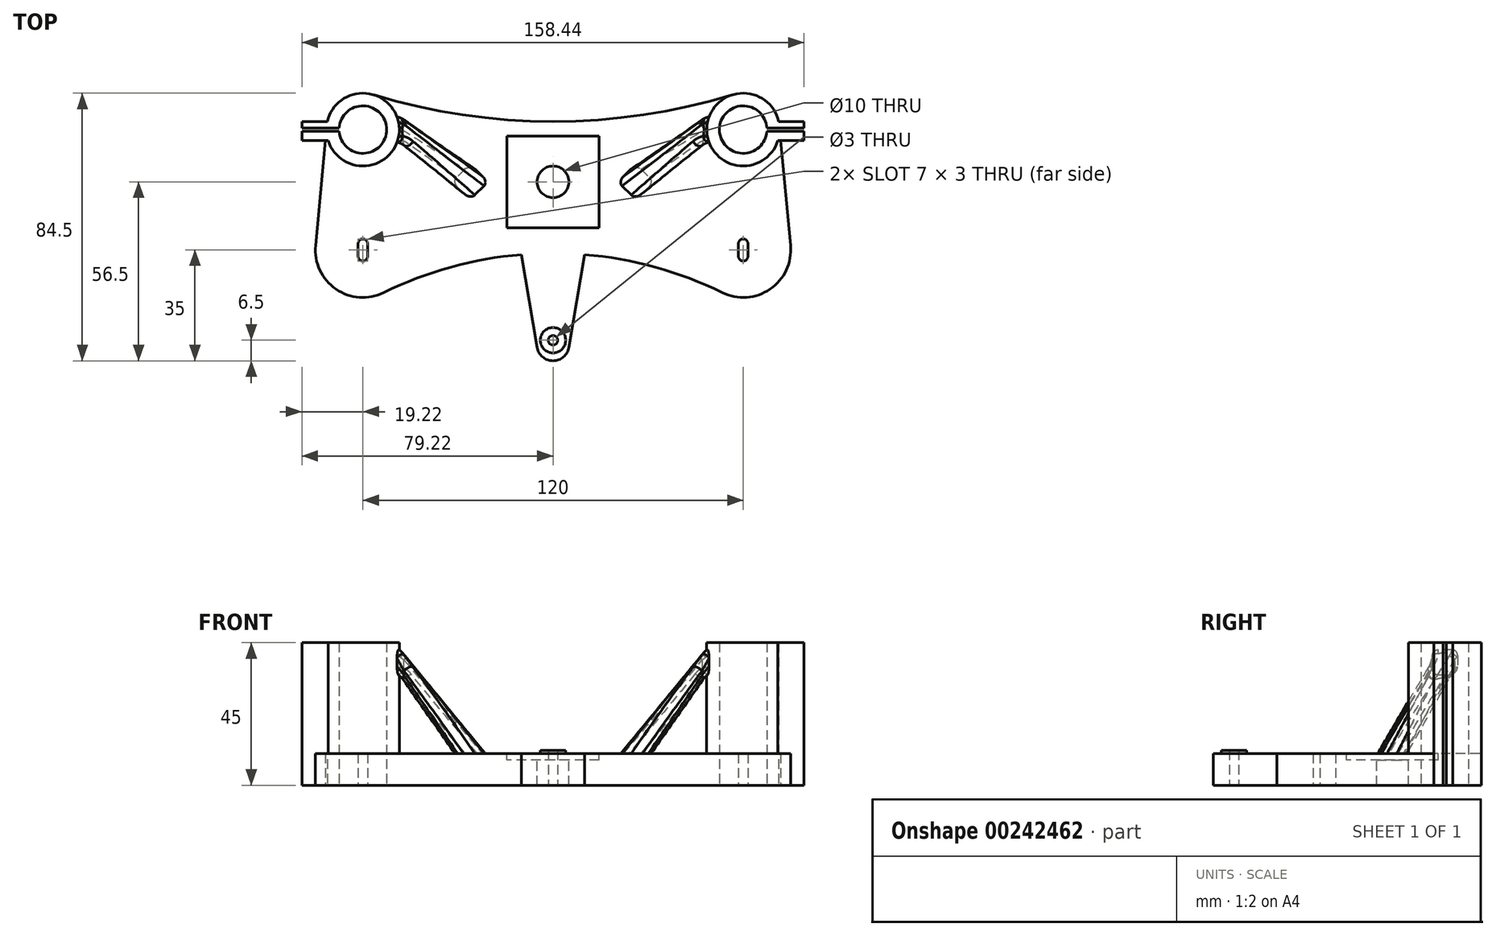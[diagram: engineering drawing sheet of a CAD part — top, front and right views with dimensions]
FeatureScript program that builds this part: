
annotation { "Feature Type Name" : "Feature", "Feature Type Description" : "" }
export const myFeature = defineFeature(function(context is Context, id is Id, definition is map)
    precondition{}
    {
        {
            var Q0;
            Q0=qCreatedBy(makeId("Top.planeOp"),FACE);
            var sketch = newSketch(context, id + "F0", { "sketchPlane" : qUnion([Q0])});
            skArc(sketch, "E0", {"start": v(-74.93, -36.6) * mm, "mid": v(-68.51, -50.35) * mm, "end": v(-53.38, -51.46) * mm});
            skArc(sketch, "E1", {"start": v(53.38, -51.46) * mm, "mid": v(68.51, -50.35) * mm, "end": v(74.93, -36.6) * mm});
            skLineSegment(sketch, "E2", {"start": v(-60, -36) * mm, "end": v(-60, -40) * mm, "construction": true});
            skLineSegment(sketch, "E3", {"start": v(60, -36) * mm, "end": v(60, -40) * mm, "construction": true});
            skArc(sketch, "E4.0.startCap", {"start": v(58.5, -36) * mm, "mid": v(60, -34.5) * mm, "end": v(61.5, -36) * mm});
            skArc(sketch, "E4.0.endCap", {"start": v(61.5, -40) * mm, "mid": v(60, -41.5) * mm, "end": v(58.5, -40) * mm});
            skLineSegment(sketch, "E4.0.left", {"start": v(61.5, -36) * mm, "end": v(61.5, -40) * mm});
            skLineSegment(sketch, "E4.0.right", {"start": v(58.5, -36) * mm, "end": v(58.5, -40) * mm});
            skArc(sketch, "E5.0.startCap", {"start": v(-61.5, -36) * mm, "mid": v(-60, -34.5) * mm, "end": v(-58.5, -36) * mm});
            skArc(sketch, "E5.0.endCap", {"start": v(-58.5, -40) * mm, "mid": v(-60, -41.5) * mm, "end": v(-61.5, -40) * mm});
            skLineSegment(sketch, "E5.0.left", {"start": v(-58.5, -36) * mm, "end": v(-58.5, -40) * mm});
            skLineSegment(sketch, "E5.0.right", {"start": v(-61.5, -36) * mm, "end": v(-61.5, -40) * mm});
            skPoint(sketch, "E6", {"position": v(0, -39.46) * mm});
            skLineSegment(sketch, "E7", {"start": v(-10, -39.46) * mm, "end": v(10, -39.46) * mm, "construction": true});
            skLineSegment(sketch, "E8", {"start": v(-10, -39.46) * mm, "end": v(-5, -68.78) * mm});
            skLineSegment(sketch, "E9", {"start": v(10, -39.46) * mm, "end": v(5, -68.78) * mm});
            skArc(sketch, "E10", {"start": v(-5, -68.78) * mm, "mid": v(0, -73) * mm, "end": v(5, -68.78) * mm});
            skLineSegment(sketch, "E11", {"start": v(-5, -68.78) * mm, "end": v(5, -68.78) * mm, "construction": true});
            skCircle(sketch, "E12", {"center": v(-60, 0) * mm, "radius": 11.5 * mm});
            skCircle(sketch, "E13", {"center": v(60, 0) * mm, "radius": 11.5 * mm});
            skLineSegment(sketch, "E14", {"start": v(-60, 0) * mm, "end": v(60, 0) * mm, "construction": true});
            skLineSegment(sketch, "E15", {"start": v(0, 0) * mm, "end": v(0, -176.53) * mm, "construction": true});
            skLineSegment(sketch, "E16", {"start": v(-60, -38) * mm, "end": v(60, -38) * mm, "construction": true});
            skLineSegment(sketch, "E17", {"start": v(-60, 0) * mm, "end": v(-60, 11.5) * mm, "construction": true});
            skLineSegment(sketch, "E18", {"start": v(60, 0) * mm, "end": v(60, 11.5) * mm, "construction": true});
            skArc(sketch, "E19", {"start": v(53.38, -51.46) * mm, "mid": v(0, -39.04) * mm, "end": v(-53.38, -51.46) * mm});
            skLineSegment(sketch, "E20", {"start": v(-56.65, 11) * mm, "end": v(56.65, 11) * mm, "construction": true});
            skArc(sketch, "E21", {"start": v(-56.65, 11) * mm, "mid": v(0, 2.56) * mm, "end": v(56.65, 11) * mm});
            skLineSegment(sketch, "E22", {"start": v(-60, 0) * mm, "end": v(-71.5, 0) * mm, "construction": true});
            skLineSegment(sketch, "E23", {"start": v(60, 0) * mm, "end": v(71.5, 0) * mm, "construction": true});
            skLineSegment(sketch, "E24", {"start": v(-71.5, 0) * mm, "end": v(-74.93, -36.6) * mm});
            skLineSegment(sketch, "E25", {"start": v(71.5, 0) * mm, "end": v(74.93, -36.6) * mm});
            skLineSegment(sketch, "E26", {"start": v(-71.22, 2.5) * mm, "end": v(-79.22, 2.5) * mm});
            skLineSegment(sketch, "E27", {"start": v(-79.22, 2.5) * mm, "end": v(-79.22, 0.5) * mm});
            skLineSegment(sketch, "E28", {"start": v(-79.22, 0.5) * mm, "end": v(-60, 0.5) * mm});
            skLineSegment(sketch, "E29", {"start": v(-60, 0.5) * mm, "end": v(-60, -0.5) * mm});
            skLineSegment(sketch, "E30", {"start": v(-60, -0.5) * mm, "end": v(-79.22, -0.5) * mm});
            skLineSegment(sketch, "E31", {"start": v(-79.22, -0.5) * mm, "end": v(-79.22, -3.5) * mm});
            skLineSegment(sketch, "E32", {"start": v(-79.22, -3.5) * mm, "end": v(-70.95, -3.5) * mm});
            skLineSegment(sketch, "E33", {"start": v(71.22, 2.5) * mm, "end": v(79.22, 2.5) * mm});
            skLineSegment(sketch, "E34", {"start": v(79.22, 2.5) * mm, "end": v(79.22, 0.5) * mm});
            skLineSegment(sketch, "E35", {"start": v(79.22, 0.5) * mm, "end": v(60, 0.5) * mm});
            skLineSegment(sketch, "E36", {"start": v(60, 0.5) * mm, "end": v(60, -0.5) * mm});
            skLineSegment(sketch, "E37", {"start": v(60, -0.5) * mm, "end": v(79.22, -0.5) * mm});
            skLineSegment(sketch, "E38", {"start": v(79.22, -0.5) * mm, "end": v(79.22, -3.5) * mm});
            skLineSegment(sketch, "E39", {"start": v(79.22, -3.5) * mm, "end": v(70.95, -3.5) * mm});
            skSolve(sketch);
        }
        {
            var Q0;
            Q0 = qSketchRegion(id + "F0", true);
            var Q1;
            Q1=makeQuery(id+"F0.imprint","IMPRINT",FACE,{"disambiguationData":[TD([[makeQuery(id+"F0.imprint","IMPRINT",EDGE,{"derivedFrom":sQuery(id+"F0.wireOp",EDGE,"LKLDyHX9-gXCm-k2y8-ggSg-qPZ12blG1iR6.bottom")}),-1.0]])]});
            extrude(context, id + "F1", {"entities" : qUnion([Q0, Q1]), "depth" : 10 * mm});
        }
        {
            var Q0;
            {var subQ0=sQuery(id+"F0.wireOp",EDGE,"E12");var subQ1=makeQuery(id+"F0.imprint","INTERSECT",VERTEX,{"derivedFrom":[subQ0,sQuery(id+"F0.wireOp",EDGE,"E21")]});Q0=makeQuery(id+"F0.imprint","IMPRINT",FACE,{"disambiguationData":[TD([[makeQuery(id+"F0.imprint","IMPRINT",EDGE,{"disambiguationData":[TD([[subQ1,-1.0]])],"derivedFrom":subQ0}),1.0]])]});}
            var Q1;
            {var subQ0=sQuery(id+"F0.wireOp",EDGE,"E13");var subQ1=makeQuery(id+"F0.imprint","INTERSECT",VERTEX,{"derivedFrom":[subQ0,sQuery(id+"F0.wireOp",EDGE,"E21")]});Q1=makeQuery(id+"F0.imprint","IMPRINT",FACE,{"disambiguationData":[TD([[makeQuery(id+"F0.imprint","IMPRINT",EDGE,{"disambiguationData":[TD([[subQ1,1.0]])],"derivedFrom":subQ0}),1.0]])]});}
            var Q2;
            {var subQ0=sQuery(id+"F0.wireOp",EDGE,"E26");Q2=makeQuery(id+"F0.imprint","IMPRINT",FACE,{"disambiguationData":[TD([[makeQuery(id+"F0.imprint","IMPRINT",EDGE,{"derivedFrom":subQ0}),1.0]])]});}
            var Q3;
            {var subQ4=sQuery(id+"F0.wireOp",EDGE,"E31");Q3=makeQuery(id+"F0.imprint","IMPRINT",FACE,{"disambiguationData":[TD([[makeQuery(id+"F0.imprint","IMPRINT",EDGE,{"derivedFrom":subQ4}),1.0]])]});}
            var Q4;
            {var subQ0=sQuery(id+"F0.wireOp",EDGE,"E32");var subQ1=sQuery(id+"F0.wireOp",EDGE,"E12");var subQ2=makeQuery(id+"F0.imprint","INTERSECT",VERTEX,{"derivedFrom":[subQ1,subQ0]});Q4=makeQuery(id+"F0.imprint","IMPRINT",FACE,{"disambiguationData":[TD([[makeQuery(id+"F0.imprint","IMPRINT",EDGE,{"disambiguationData":[TD([[subQ2,1.0]])],"derivedFrom":subQ1}),-1.0]])]});}
            var Q5;
            {var subQ0=sQuery(id+"F0.wireOp",EDGE,"E39");var subQ1=sQuery(id+"F0.wireOp",EDGE,"E13");var subQ2=makeQuery(id+"F0.imprint","INTERSECT",VERTEX,{"derivedFrom":[subQ1,subQ0]});Q5=makeQuery(id+"F0.imprint","IMPRINT",FACE,{"disambiguationData":[TD([[makeQuery(id+"F0.imprint","IMPRINT",EDGE,{"disambiguationData":[TD([[subQ2,-1.0]])],"derivedFrom":subQ1}),-1.0]])]});}
            var Q6;
            {var subQ5=sQuery(id+"F0.wireOp",EDGE,"E38");Q6=makeQuery(id+"F0.imprint","IMPRINT",FACE,{"disambiguationData":[TD([[makeQuery(id+"F0.imprint","IMPRINT",EDGE,{"derivedFrom":subQ5}),-1.0]])]});}
            var Q7;
            {var subQ0=sQuery(id+"F0.wireOp",EDGE,"E33");Q7=makeQuery(id+"F0.imprint","IMPRINT",FACE,{"disambiguationData":[TD([[makeQuery(id+"F0.imprint","IMPRINT",EDGE,{"derivedFrom":subQ0}),-1.0]])]});}
            extrude(context, id + "F2", {"entities" : qUnion([Q0, Q1, Q2, Q3, Q4, Q5, Q6, Q7]), "operationType" : NewBodyOperationType.ADD, "depth" : 45 * mm});
        }
        {
            var Q0;
            Q0=makeQuery(id+"F1.opExtrude","CAP_FACE",FACE,{"disambiguationData":[OSD([sQuery(id+"F0.wireOp",EDGE,"47a20475-fb0e-48b2-b259-d4306b60a212"),sQuery(id+"F0.wireOp",EDGE,"11a2ab9f-6c47-45e5-a705-5a51ec2baa43"),sQuery(id+"F0.wireOp",EDGE,"7d5b429a-6b9c-4788-a966-0b9b0a1ef2b6"),sQuery(id+"F0.wireOp",EDGE,"E0"),sQuery(id+"F0.wireOp",EDGE,"E1"),sQuery(id+"F0.wireOp",EDGE,"E4.0.startCap"),sQuery(id+"F0.wireOp",EDGE,"E4.0.endCap"),sQuery(id+"F0.wireOp",EDGE,"E4.0.left"),sQuery(id+"F0.wireOp",EDGE,"E4.0.right"),sQuery(id+"F0.wireOp",EDGE,"E5.0.startCap"),sQuery(id+"F0.wireOp",EDGE,"E5.0.endCap"),sQuery(id+"F0.wireOp",EDGE,"E5.0.left"),sQuery(id+"F0.wireOp",EDGE,"E5.0.right"),sQuery(id+"F0.wireOp",EDGE,"ed3533a6-83fa-43d6-bacc-5741e4b977db"),sQuery(id+"F0.wireOp",EDGE,"E8"),sQuery(id+"F0.wireOp",EDGE,"E9"),sQuery(id+"F0.wireOp",EDGE,"E10"),sQuery(id+"F0.wireOp",EDGE,"E12"),sQuery(id+"F0.wireOp",EDGE,"E13")])],"isStart":true});
            var sketch = newSketch(context, id + "F3", { "sketchPlane" : qUnion([Q0])});
            skCircle(sketch, "E40", {"center": v(-60, 0) * mm, "radius": 7.5 * mm});
            skCircle(sketch, "E41", {"center": v(60, 0) * mm, "radius": 7.5 * mm});
            skSolve(sketch);
        }
        {
            var Q0;
            Q0 = qSketchRegion(id + "F3", true);
            var Q1;
            {var subQ0=sQuery(id+"F0.wireOp",EDGE,"E29");Q1=makeQuery(id+"F0.imprint","IMPRINT",FACE,{"disambiguationData":[TD([[makeQuery(id+"F0.imprint","IMPRINT",EDGE,{"derivedFrom":subQ0}),-1.0]])]});}
            var Q2;
            {var subQ0=sQuery(id+"F0.wireOp",EDGE,"E24");var subQ1=sQuery(id+"F0.wireOp",EDGE,"E12");var subQ2=makeQuery(id+"F0.imprint","INTERSECT",VERTEX,{"derivedFrom":[subQ1,subQ0]});Q2=makeQuery(id+"F0.imprint","IMPRINT",FACE,{"disambiguationData":[TD([[makeQuery(id+"F0.imprint","IMPRINT",EDGE,{"disambiguationData":[TD([[subQ2,-1.0]])],"derivedFrom":subQ1}),-1.0]])]});}
            var Q3;
            {var subQ0=sQuery(id+"F0.wireOp",EDGE,"E36");Q3=makeQuery(id+"F0.imprint","IMPRINT",FACE,{"disambiguationData":[TD([[makeQuery(id+"F0.imprint","IMPRINT",EDGE,{"derivedFrom":subQ0}),1.0]])]});}
            var Q4;
            {var subQ0=sQuery(id+"F0.wireOp",EDGE,"E25");var subQ1=sQuery(id+"F0.wireOp",EDGE,"E13");var subQ2=makeQuery(id+"F0.imprint","INTERSECT",VERTEX,{"derivedFrom":[subQ1,subQ0]});Q4=makeQuery(id+"F0.imprint","IMPRINT",FACE,{"disambiguationData":[TD([[makeQuery(id+"F0.imprint","IMPRINT",EDGE,{"disambiguationData":[TD([[subQ2,1.0]])],"derivedFrom":subQ1}),-1.0]])]});}
            extrude(context, id + "F4", {"entities" : qUnion([Q0, Q1, Q2, Q3, Q4]), "operationType" : NewBodyOperationType.REMOVE, "endBound" : BoundingType.THROUGH_ALL, "oppositeDirection" : true, "depth" : 25 * mm});
        }
        {
            var Q0;
            Q0=makeQuery(id+"F1.opExtrude","CAP_FACE",FACE,{"disambiguationData":[OSD([sQuery(id+"F0.wireOp",EDGE,"E0"),sQuery(id+"F0.wireOp",EDGE,"E1"),sQuery(id+"F0.wireOp",EDGE,"E4.0.startCap"),sQuery(id+"F0.wireOp",EDGE,"E4.0.endCap"),sQuery(id+"F0.wireOp",EDGE,"E4.0.left"),sQuery(id+"F0.wireOp",EDGE,"E4.0.right"),sQuery(id+"F0.wireOp",EDGE,"E5.0.startCap"),sQuery(id+"F0.wireOp",EDGE,"E5.0.endCap"),sQuery(id+"F0.wireOp",EDGE,"E5.0.left"),sQuery(id+"F0.wireOp",EDGE,"E5.0.right"),sQuery(id+"F0.wireOp",EDGE,"E8"),sQuery(id+"F0.wireOp",EDGE,"E9"),sQuery(id+"F0.wireOp",EDGE,"E10"),sQuery(id+"F0.wireOp",EDGE,"E12"),sQuery(id+"F0.wireOp",EDGE,"E13"),sQuery(id+"F0.wireOp",EDGE,"E19"),sQuery(id+"F0.wireOp",EDGE,"E21"),sQuery(id+"F0.wireOp",EDGE,"E24"),sQuery(id+"F0.wireOp",EDGE,"E25")])],"isStart":false});
            var sketch = newSketch(context, id + "F5", { "sketchPlane" : qUnion([Q0])});
            skCircle(sketch, "E42", {"center": v(0, -16.5) * mm, "radius": 5 * mm});
            skLineSegment(sketch, "E43.bottom", {"start": v(14.5, -2) * mm, "end": v(-14.5, -2) * mm});
            skLineSegment(sketch, "E43.top", {"start": v(14.5, -31) * mm, "end": v(-14.5, -31) * mm});
            skLineSegment(sketch, "E43.left", {"start": v(14.5, -2) * mm, "end": v(14.5, -31) * mm});
            skLineSegment(sketch, "E43.right", {"start": v(-14.5, -2) * mm, "end": v(-14.5, -31) * mm});
            skSolve(sketch);
        }
        {
            var Q0;
            Q0=makeQuery(id+"F5.imprint","IMPRINT",FACE,{"disambiguationData":[TD([[makeQuery(id+"F5.imprint","IMPRINT",EDGE,{"derivedFrom":sQuery(id+"F5.wireOp",EDGE,"E42")}),1.0]])]});
            extrude(context, id + "F6", {"entities" : qUnion([Q0]), "operationType" : NewBodyOperationType.REMOVE, "endBound" : BoundingType.THROUGH_ALL, "oppositeDirection" : true, "depth" : 25 * mm});
        }
        {
            var Q0;
            Q0=makeQuery(id+"F5.imprint","IMPRINT",FACE,{"disambiguationData":[TD([[makeQuery(id+"F5.imprint","IMPRINT",EDGE,{"derivedFrom":sQuery(id+"F5.wireOp",EDGE,"E42")}),-1.0]])]});
            extrude(context, id + "F7", {"entities" : qUnion([Q0]), "operationType" : NewBodyOperationType.REMOVE, "oppositeDirection" : true, "depth" : 2 * mm});
        }
        {
            var Q0;
            Q0=qCreatedBy(makeId("Right.planeOp"),FACE);
            var sketch = newSketch(context, id + "F8", { "sketchPlane" : qUnion([Q0])});
            skLineSegment(sketch, "E44.bottom", {"start": v(-4, 42.81) * mm, "end": v(4, 42.81) * mm});
            skLineSegment(sketch, "E44.top", {"start": v(-4, 34.81) * mm, "end": v(4, 34.81) * mm});
            skLineSegment(sketch, "E44.left", {"start": v(-4, 42.81) * mm, "end": v(-4, 34.81) * mm});
            skLineSegment(sketch, "E44.right", {"start": v(4, 42.81) * mm, "end": v(4, 34.81) * mm});
            skPoint(sketch, "E45", {"position": v(0, 42.81) * mm});
            skSolve(sketch);
        }
        {
            var Q0;
            {var subQ0=sQuery(id+"F0.wireOp",EDGE,"E25");var subQ1=sQuery(id+"F0.wireOp",EDGE,"E1");var subQ2=sQuery(id+"F0.wireOp",EDGE,"E39");var subQ3=sQuery(id+"F0.wireOp",EDGE,"E12");var subQ4=sQuery(id+"F0.wireOp",EDGE,"E21");var subQ5=sQuery(id+"F0.wireOp",EDGE,"E19");var subQ6=sQuery(id+"F0.wireOp",EDGE,"E0");var subQ7=sQuery(id+"F0.wireOp",EDGE,"E8");var subQ8=sQuery(id+"F0.wireOp",EDGE,"E9");var subQ9=sQuery(id+"F0.wireOp",EDGE,"E13");var subQ10=sQuery(id+"F0.wireOp",EDGE,"E33");var subQ11=sQuery(id+"F0.wireOp",EDGE,"E26");var subQ12=sQuery(id+"F0.wireOp",EDGE,"E32");var subQ13=sQuery(id+"F0.wireOp",EDGE,"E10");var subQ14=sQuery(id+"F0.wireOp",EDGE,"E4.0.startCap");var subQ15=sQuery(id+"F0.wireOp",EDGE,"E4.0.endCap");var subQ16=sQuery(id+"F0.wireOp",EDGE,"E24");var subQ17=sQuery(id+"F0.wireOp",EDGE,"E5.0.right");var subQ18=sQuery(id+"F0.wireOp",EDGE,"E4.0.left");var subQ19=sQuery(id+"F0.wireOp",EDGE,"E4.0.right");var subQ20=sQuery(id+"F0.wireOp",EDGE,"E5.0.startCap");var subQ21=sQuery(id+"F0.wireOp",EDGE,"E5.0.endCap");var subQ22=sQuery(id+"F0.wireOp",EDGE,"E5.0.left");Q0=makeQuery(id+"F2.boolean.opBoolean","SPLIT",FACE,{"disambiguationData":[TD([makeQuery(id+"F1.opExtrude","SWEPT_FACE",FACE,{"disambiguationData":[OSD([subQ6])]})])],"derivedFrom":makeQuery(id+"F1.opExtrude","CAP_FACE",FACE,{"disambiguationData":[OSD([subQ6,subQ1,subQ14,subQ15,subQ18,subQ19,subQ20,subQ21,subQ22,subQ17,subQ7,subQ8,subQ13,subQ3,subQ9,subQ5,subQ4,subQ16,subQ0,subQ11,sQuery(id+"F0.wireOp",EDGE,"E27"),sQuery(id+"F0.wireOp",EDGE,"E28"),sQuery(id+"F0.wireOp",EDGE,"E30"),sQuery(id+"F0.wireOp",EDGE,"E31"),subQ12,subQ10,sQuery(id+"F0.wireOp",EDGE,"E34"),sQuery(id+"F0.wireOp",EDGE,"E35"),sQuery(id+"F0.wireOp",EDGE,"E37"),sQuery(id+"F0.wireOp",EDGE,"E38"),subQ2])],"isStart":false})});}
            var sketch = newSketch(context, id + "F9", { "sketchPlane" : qUnion([Q0])});
            skLineSegment(sketch, "E46.bottom", {"start": v(20.5, -16.5) * mm, "end": v(26.16, -10.84) * mm});
            skLineSegment(sketch, "E46.top", {"start": v(26.16, -22.16) * mm, "end": v(31.81, -16.5) * mm});
            skLineSegment(sketch, "E46.left", {"start": v(20.5, -16.5) * mm, "end": v(26.16, -22.16) * mm});
            skLineSegment(sketch, "E46.right", {"start": v(26.16, -10.84) * mm, "end": v(31.81, -16.5) * mm});
            skLineSegment(sketch, "E47", {"start": v(26.16, -22.16) * mm, "end": v(26.16, -10.84) * mm, "construction": true});
            skLineSegment(sketch, "E48.bottom", {"start": v(-26.16, -10.84) * mm, "end": v(-20.5, -16.5) * mm});
            skLineSegment(sketch, "E48.top", {"start": v(-31.81, -16.5) * mm, "end": v(-26.16, -22.16) * mm});
            skLineSegment(sketch, "E48.left", {"start": v(-26.16, -10.84) * mm, "end": v(-31.81, -16.5) * mm});
            skLineSegment(sketch, "E48.right", {"start": v(-20.5, -16.5) * mm, "end": v(-26.16, -22.16) * mm});
            skLineSegment(sketch, "E49", {"start": v(-26.16, -10.84) * mm, "end": v(-26.16, -22.16) * mm, "construction": true});
            skCircle(sketch, "E50", {"center": v(0, -66.5) * mm, "radius": 4 * mm});
            skCircle(sketch, "E51", {"center": v(0, -66.5) * mm, "radius": 1.5 * mm});
            skSolve(sketch);
        }
        {
            var Q0;
            Q0 = qSketchRegion(id + "F8", true);
            var Q1;
            {var subQ0=sQuery(id+"F0.wireOp",EDGE,"E13");Q1=makeQuery(id+"F2.boolean.opBoolean","MERGE",FACE,{"derivedFrom":[makeQuery(id+"F1.opExtrude","SWEPT_FACE",FACE,{"disambiguationData":[OSD([subQ0]),TDD([makeQuery(id+"F0.imprint","IMPRINT",EDGE,{"disambiguationData":[TD([[makeQuery(id+"F0.imprint","INTERSECT",VERTEX,{"derivedFrom":[subQ0,sQuery(id+"F0.wireOp",EDGE,"E21")]}),1.0]])],"derivedFrom":subQ0})])]}),makeQuery(id+"F2.opExtrude","SWEPT_FACE",FACE,{"disambiguationData":[OSD([subQ0])]})]});}
            var Q2;
            {var subQ0=sQuery(id+"F0.wireOp",EDGE,"E13");Q2=makeQuery(id+"F2.boolean.opBoolean","MERGE",FACE,{"derivedFrom":[makeQuery(id+"F1.opExtrude","SWEPT_FACE",FACE,{"disambiguationData":[OSD([subQ0]),TDD([makeQuery(id+"F0.imprint","IMPRINT",EDGE,{"disambiguationData":[TD([[makeQuery(id+"F0.imprint","INTERSECT",VERTEX,{"derivedFrom":[subQ0,sQuery(id+"F0.wireOp",EDGE,"E21")]}),1.0]])],"derivedFrom":subQ0})])]}),makeQuery(id+"F2.opExtrude","SWEPT_FACE",FACE,{"disambiguationData":[OSD([subQ0])]})]});}
            extrude(context, id + "F10", {"entities" : qUnion([Q0]), "operationType" : NewBodyOperationType.ADD, "endBound" : BoundingType.UP_TO_SURFACE, "endBoundEntityFace" : qUnion([Q1]), "depth" : 25 * mm, "hasSecondDirection" : true, "secondDirectionOppositeDirection" : false, "secondDirectionBoundEntityFace" : qUnion([Q2]), "secondDirectionDepth" : 48.3 * mm});
        }
        {
            var Q0;
            Q0=makeQuery(id+"F8.imprint","IMPRINT",FACE,{"disambiguationData":[TD([[makeQuery(id+"F8.imprint","IMPRINT",EDGE,{"derivedFrom":sQuery(id+"F8.wireOp",EDGE,"E44.bottom")}),-1.0]])]});
            var Q1;
            {var subQ0=sQuery(id+"F0.wireOp",EDGE,"E12");Q1=makeQuery(id+"F2.boolean.opBoolean","MERGE",FACE,{"derivedFrom":[makeQuery(id+"F1.opExtrude","SWEPT_FACE",FACE,{"disambiguationData":[OSD([subQ0]),TDD([makeQuery(id+"F0.imprint","IMPRINT",EDGE,{"disambiguationData":[TD([[makeQuery(id+"F0.imprint","INTERSECT",VERTEX,{"derivedFrom":[subQ0,sQuery(id+"F0.wireOp",EDGE,"E21")]}),-1.0]])],"derivedFrom":subQ0})])]}),makeQuery(id+"F2.opExtrude","SWEPT_FACE",FACE,{"disambiguationData":[OSD([subQ0])]})]});}
            extrude(context, id + "F11", {"entities" : qUnion([Q0]), "operationType" : NewBodyOperationType.ADD, "endBound" : BoundingType.UP_TO_SURFACE, "oppositeDirection" : true, "endBoundEntityFace" : qUnion([Q1]), "depth" : 46.6 * mm, "hasSecondDirection" : true, "secondDirectionOppositeDirection" : true, "secondDirectionDepth" : 48.3 * mm});
        }
        {
            var Q1;
            Q1=makeQuery(id+"F9.imprint","IMPRINT",FACE,{"disambiguationData":[TD([[makeQuery(id+"F9.imprint","IMPRINT",EDGE,{"derivedFrom":sQuery(id+"F9.wireOp",EDGE,"E46.bottom")}),-1.0]])]});
            var Q2;
            Q2=makeQuery(id+"F10.opExtrude","CAP_FACE",FACE,{"disambiguationData":[OSD([sQuery(id+"F8.wireOp",EDGE,"E44.bottom"),sQuery(id+"F8.wireOp",EDGE,"E44.top"),sQuery(id+"F8.wireOp",EDGE,"E44.left"),sQuery(id+"F8.wireOp",EDGE,"E44.right")])],"isStart":true});
            loft(context, id + "F12", {"operationType" : NewBodyOperationType.ADD, "sheetProfilesArray" : [{ "sheetProfileEntities" : qUnion([Q1]) }, { "sheetProfileEntities" : qUnion([Q2]) }]});
        }
        {
            var Q1;
            Q1=makeQuery(id+"F9.imprint","IMPRINT",FACE,{"disambiguationData":[TD([[makeQuery(id+"F9.imprint","IMPRINT",EDGE,{"derivedFrom":sQuery(id+"F9.wireOp",EDGE,"E48.bottom")}),-1.0]])]});
            var Q2;
            Q2=makeQuery(id+"F11.opExtrude","CAP_FACE",FACE,{"disambiguationData":[OSD([sQuery(id+"F8.wireOp",EDGE,"E44.bottom"),sQuery(id+"F8.wireOp",EDGE,"E44.top"),sQuery(id+"F8.wireOp",EDGE,"E44.left"),sQuery(id+"F8.wireOp",EDGE,"E44.right")])],"isStart":true});
            loft(context, id + "F13", {"operationType" : NewBodyOperationType.ADD, "sheetProfilesArray" : [{ "sheetProfileEntities" : qUnion([Q1]) }, { "sheetProfileEntities" : qUnion([Q2]) }]});
        }
        {
            var Q0;
            {var subQ0=sQuery(id+"F8.wireOp",EDGE,"E44.right");Q0=makeQuery(id+"F12.boolean.opBoolean","MERGE",EDGE,{"derivedFrom":[makeQuery(id+"F10.opExtrude","CAP_EDGE",EDGE,{"disambiguationData":[OSD([subQ0])],"isStart":true}),makeQuery(id+"F12.opLoft","MID_CAP_EDGE",EDGE,{"disambiguationData":[OSD([sQuery(id+"F8.wireOp",EDGE,"E44.bottom"),sQuery(id+"F8.wireOp",EDGE,"E44.top"),subQ0])],"capPos":1.0})]});}
            var Q1;
            {var subQ0=sQuery(id+"F8.wireOp",EDGE,"E44.left");Q1=makeQuery(id+"F12.boolean.opBoolean","MERGE",EDGE,{"derivedFrom":[makeQuery(id+"F10.opExtrude","CAP_EDGE",EDGE,{"disambiguationData":[OSD([subQ0])],"isStart":true}),makeQuery(id+"F12.opLoft","MID_CAP_EDGE",EDGE,{"disambiguationData":[OSD([sQuery(id+"F8.wireOp",EDGE,"E44.bottom"),sQuery(id+"F8.wireOp",EDGE,"E44.top"),subQ0])],"capPos":1.0})]});}
            var Q2;
            {var subQ0=sQuery(id+"F8.wireOp",EDGE,"E44.bottom");Q2=makeQuery(id+"F12.boolean.opBoolean","MERGE",EDGE,{"derivedFrom":[makeQuery(id+"F10.opExtrude","CAP_EDGE",EDGE,{"disambiguationData":[OSD([subQ0])],"isStart":true}),makeQuery(id+"F12.opLoft","MID_CAP_EDGE",EDGE,{"disambiguationData":[OSD([subQ0,sQuery(id+"F8.wireOp",EDGE,"E44.left"),sQuery(id+"F8.wireOp",EDGE,"E44.right")])],"capPos":1.0})]});}
            var Q3;
            {var subQ0=sQuery(id+"F8.wireOp",EDGE,"E44.bottom");Q3=makeQuery(id+"F13.boolean.opBoolean","MERGE",EDGE,{"derivedFrom":[makeQuery(id+"F11.opExtrude","CAP_EDGE",EDGE,{"disambiguationData":[OSD([subQ0])],"isStart":true}),makeQuery(id+"F13.opLoft","MID_CAP_EDGE",EDGE,{"disambiguationData":[OSD([subQ0,sQuery(id+"F8.wireOp",EDGE,"E44.left"),sQuery(id+"F8.wireOp",EDGE,"E44.right")])],"capPos":1.0})]});}
            var Q4;
            {var subQ0=sQuery(id+"F8.wireOp",EDGE,"E44.left");Q4=makeQuery(id+"F13.boolean.opBoolean","MERGE",EDGE,{"derivedFrom":[makeQuery(id+"F11.opExtrude","CAP_EDGE",EDGE,{"disambiguationData":[OSD([subQ0])],"isStart":true}),makeQuery(id+"F13.opLoft","MID_CAP_EDGE",EDGE,{"disambiguationData":[OSD([sQuery(id+"F8.wireOp",EDGE,"E44.bottom"),sQuery(id+"F8.wireOp",EDGE,"E44.top"),subQ0])],"capPos":1.0})]});}
            var Q5;
            {var subQ0=sQuery(id+"F8.wireOp",EDGE,"E44.right");Q5=makeQuery(id+"F13.boolean.opBoolean","MERGE",EDGE,{"derivedFrom":[makeQuery(id+"F11.opExtrude","CAP_EDGE",EDGE,{"disambiguationData":[OSD([subQ0])],"isStart":true}),makeQuery(id+"F13.opLoft","MID_CAP_EDGE",EDGE,{"disambiguationData":[OSD([sQuery(id+"F8.wireOp",EDGE,"E44.bottom"),sQuery(id+"F8.wireOp",EDGE,"E44.top"),subQ0])],"capPos":1.0})]});}
            var Q6;
            {var subQ0=sQuery(id+"F8.wireOp",EDGE,"E44.top");Q6=makeQuery(id+"F13.boolean.opBoolean","MERGE",EDGE,{"derivedFrom":[makeQuery(id+"F11.opExtrude","CAP_EDGE",EDGE,{"disambiguationData":[OSD([subQ0])],"isStart":true}),makeQuery(id+"F13.opLoft","MID_CAP_EDGE",EDGE,{"disambiguationData":[OSD([subQ0,sQuery(id+"F8.wireOp",EDGE,"E44.left"),sQuery(id+"F8.wireOp",EDGE,"E44.right")])],"capPos":1.0})]});}
            var Q7;
            {var subQ0=sQuery(id+"F8.wireOp",EDGE,"E44.top");Q7=makeQuery(id+"F12.boolean.opBoolean","MERGE",EDGE,{"derivedFrom":[makeQuery(id+"F10.opExtrude","CAP_EDGE",EDGE,{"disambiguationData":[OSD([subQ0])],"isStart":true}),makeQuery(id+"F12.opLoft","MID_CAP_EDGE",EDGE,{"disambiguationData":[OSD([subQ0,sQuery(id+"F8.wireOp",EDGE,"E44.left"),sQuery(id+"F8.wireOp",EDGE,"E44.right")])],"capPos":1.0})]});}
            fillet(context, id + "F14", {"entities" : qUnion([Q0, Q1, Q2, Q3, Q4, Q5, Q6, Q7]), "radius" : 5 * mm, "tangentPropagation" : true, "allowEdgeOverflow" : false});
        }
        {
            var Q0;
            Q0=makeQuery(id+"F12.opLoft","SWEPT_EDGE",EDGE,{"disambiguationData":[OSD([sQuery(id+"F8.wireOp",EDGE,"E44.bottom"),sQuery(id+"F8.wireOp",EDGE,"E44.right"),sQuery(id+"F9.wireOp",EDGE,"E46.bottom"),sQuery(id+"F9.wireOp",EDGE,"E46.left")])]});
            var Q1;
            Q1=makeQuery(id+"F12.opLoft","SWEPT_EDGE",EDGE,{"disambiguationData":[OSD([sQuery(id+"F8.wireOp",EDGE,"E44.bottom"),sQuery(id+"F8.wireOp",EDGE,"E44.left"),sQuery(id+"F9.wireOp",EDGE,"E46.top"),sQuery(id+"F9.wireOp",EDGE,"E46.left")])]});
            var Q2;
            Q2=makeQuery(id+"F12.opLoft","SWEPT_EDGE",EDGE,{"disambiguationData":[OSD([sQuery(id+"F8.wireOp",EDGE,"E44.top"),sQuery(id+"F8.wireOp",EDGE,"E44.right"),sQuery(id+"F9.wireOp",EDGE,"E46.bottom"),sQuery(id+"F9.wireOp",EDGE,"E46.right")])]});
            var Q3;
            Q3=makeQuery(id+"F12.opLoft","MID_CAP_EDGE",EDGE,{"disambiguationData":[OSD([sQuery(id+"F9.wireOp",EDGE,"E46.bottom"),sQuery(id+"F9.wireOp",EDGE,"E46.left"),sQuery(id+"F9.wireOp",EDGE,"E46.right")])],"capPos":0.0});
            var Q4;
            Q4=makeQuery(id+"F12.opLoft","SWEPT_EDGE",EDGE,{"disambiguationData":[OSD([sQuery(id+"F8.wireOp",EDGE,"E44.top"),sQuery(id+"F8.wireOp",EDGE,"E44.left"),sQuery(id+"F9.wireOp",EDGE,"E46.top"),sQuery(id+"F9.wireOp",EDGE,"E46.right")])]});
            var Q5;
            Q5=makeQuery(id+"F13.opLoft","SWEPT_EDGE",EDGE,{"disambiguationData":[OSD([sQuery(id+"F8.wireOp",EDGE,"E44.bottom"),sQuery(id+"F8.wireOp",EDGE,"E44.right"),sQuery(id+"F9.wireOp",EDGE,"E48.bottom"),sQuery(id+"F9.wireOp",EDGE,"E48.right")])]});
            var Q6;
            Q6=makeQuery(id+"F13.opLoft","MID_CAP_EDGE",EDGE,{"disambiguationData":[OSD([sQuery(id+"F9.wireOp",EDGE,"E48.bottom"),sQuery(id+"F9.wireOp",EDGE,"E48.top"),sQuery(id+"F9.wireOp",EDGE,"E48.right")])],"capPos":0.0});
            var Q7;
            Q7=makeQuery(id+"F13.opLoft","MID_CAP_EDGE",EDGE,{"disambiguationData":[OSD([sQuery(id+"F9.wireOp",EDGE,"E48.top"),sQuery(id+"F9.wireOp",EDGE,"E48.left"),sQuery(id+"F9.wireOp",EDGE,"E48.right")])],"capPos":0.0});
            var Q8;
            Q8=makeQuery(id+"F13.opLoft","SWEPT_EDGE",EDGE,{"disambiguationData":[OSD([sQuery(id+"F8.wireOp",EDGE,"E44.top"),sQuery(id+"F8.wireOp",EDGE,"E44.left"),sQuery(id+"F9.wireOp",EDGE,"E48.top"),sQuery(id+"F9.wireOp",EDGE,"E48.left")])]});
            var Q9;
            Q9=makeQuery(id+"F13.opLoft","SWEPT_EDGE",EDGE,{"disambiguationData":[OSD([sQuery(id+"F8.wireOp",EDGE,"E44.top"),sQuery(id+"F8.wireOp",EDGE,"E44.right"),sQuery(id+"F9.wireOp",EDGE,"E48.bottom"),sQuery(id+"F9.wireOp",EDGE,"E48.left")])]});
            var Q10;
            Q10=makeQuery(id+"F13.opLoft","SWEPT_EDGE",EDGE,{"disambiguationData":[OSD([sQuery(id+"F8.wireOp",EDGE,"E44.bottom"),sQuery(id+"F8.wireOp",EDGE,"E44.left"),sQuery(id+"F9.wireOp",EDGE,"E48.top"),sQuery(id+"F9.wireOp",EDGE,"E48.right")])]});
            fillet(context, id + "F15", {"entities" : qUnion([Q0, Q1, Q2, Q3, Q4, Q5, Q6, Q7, Q8, Q9, Q10]), "radius" : 2 * mm, "tangentPropagation" : true, "allowEdgeOverflow" : false});
        }
        {
            var Q0;
            Q0=makeQuery(id+"F9.imprint","IMPRINT",FACE,{"disambiguationData":[TD([[makeQuery(id+"F9.imprint","IMPRINT",EDGE,{"derivedFrom":sQuery(id+"F9.wireOp",EDGE,"E50")}),1.0]])]});
            extrude(context, id + "F16", {"entities" : qUnion([Q0]), "operationType" : NewBodyOperationType.ADD, "depth" : 1 * mm});
        }
        {
            var Q0;
            Q0=makeQuery(id+"F9.imprint","IMPRINT",FACE,{"disambiguationData":[TD([[makeQuery(id+"F9.imprint","IMPRINT",EDGE,{"derivedFrom":sQuery(id+"F9.wireOp",EDGE,"E51")}),1.0]])]});
            extrude(context, id + "F17", {"entities" : qUnion([Q0]), "operationType" : NewBodyOperationType.REMOVE, "endBound" : BoundingType.UP_TO_NEXT, "oppositeDirection" : true, "depth" : 25 * mm});
        }
    });
